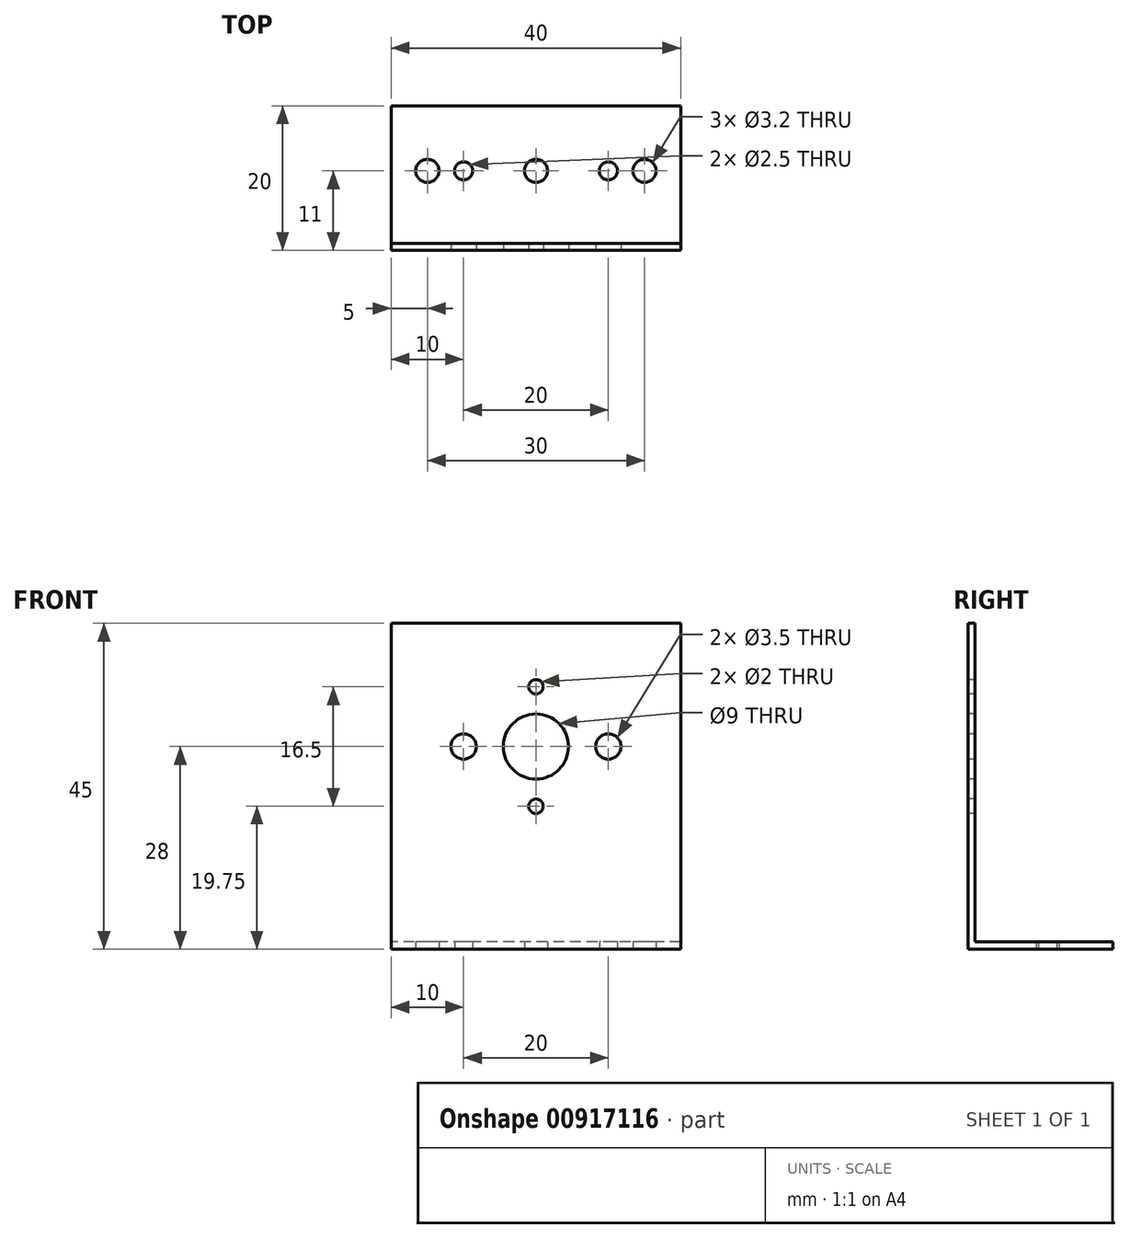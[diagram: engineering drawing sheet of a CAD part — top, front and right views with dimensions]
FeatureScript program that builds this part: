
annotation { "Feature Type Name" : "Feature", "Feature Type Description" : "" }
export const myFeature = defineFeature(function(context is Context, id is Id, definition is map)
    precondition{}
    {
        {
            var Q0;
            Q0=qCreatedBy(makeId("Right.planeOp"),FACE);
            var sketch = newSketch(context, id + "F0", { "sketchPlane" : qUnion([Q0])});
            skLineSegment(sketch, "E0", {"start": v(0, 0) * mm, "end": v(0, 45) * mm});
            skLineSegment(sketch, "E1", {"start": v(0, 45) * mm, "end": v(1, 45) * mm});
            skLineSegment(sketch, "E2", {"start": v(1, 45) * mm, "end": v(1, 1) * mm});
            skLineSegment(sketch, "E3", {"start": v(1, 1) * mm, "end": v(20, 1) * mm});
            skLineSegment(sketch, "E4", {"start": v(20, 1) * mm, "end": v(20, 0) * mm});
            skLineSegment(sketch, "E5", {"start": v(20, 0) * mm, "end": v(0, 0) * mm});
            skSolve(sketch);
        }
        {
            var Q0;
            Q0=makeQuery(id+"F0.imprint","IMPRINT",FACE,{"disambiguationData":[TD([[makeQuery(id+"F0.imprint","IMPRINT",EDGE,{"derivedFrom":sQuery(id+"F0.wireOp",EDGE,"E0")}),-1.0]])]});
            extrude(context, id + "F1", {"entities" : qUnion([Q0]), "depth" : 40 * mm, "offsetDistance" : 25.4 * mm});
        }
        {
            var Q0;
            Q0=makeQuery(id+"F1.opExtrude","SWEPT_FACE",FACE,{"disambiguationData":[OSD([sQuery(id+"F0.wireOp",EDGE,"E5")])]});
            var sketch = newSketch(context, id + "F2", { "sketchPlane" : qUnion([Q0])});
            skCircle(sketch, "E6", {"center": v(5, -11) * mm, "radius": 1.6 * mm});
            skCircle(sketch, "E7", {"center": v(10, -11) * mm, "radius": 1.25 * mm});
            skCircle(sketch, "E8", {"center": v(20, -11) * mm, "radius": 1.6 * mm});
            skCircle(sketch, "E9", {"center": v(30, -11) * mm, "radius": 1.25 * mm});
            skCircle(sketch, "E10", {"center": v(35, -11) * mm, "radius": 1.6 * mm});
            skPoint(sketch, "E11", {"position": v(20, 0) * mm});
            skSolve(sketch);
        }
        {
            var Q0;
            Q0=makeQuery(id+"F1.opExtrude","SWEPT_FACE",FACE,{"disambiguationData":[OSD([sQuery(id+"F0.wireOp",EDGE,"E0")])]});
            var sketch = newSketch(context, id + "F3", { "sketchPlane" : qUnion([Q0])});
            skCircle(sketch, "E12", {"center": v(20, 28) * mm, "radius": 4.5 * mm});
            skCircle(sketch, "E13", {"center": v(20, 36.25) * mm, "radius": 1 * mm});
            skCircle(sketch, "E14", {"center": v(20, 19.75) * mm, "radius": 1 * mm});
            skCircle(sketch, "E15", {"center": v(30, 28) * mm, "radius": 1.75 * mm});
            skCircle(sketch, "E16", {"center": v(10, 28) * mm, "radius": 1.75 * mm});
            skLineSegment(sketch, "E17", {"start": v(20, 36.25) * mm, "end": v(20, 19.75) * mm, "construction": true});
            skLineSegment(sketch, "E18", {"start": v(10, 28) * mm, "end": v(30, 28) * mm, "construction": true});
            skLineSegment(sketch, "E19", {"start": v(20, 45) * mm, "end": v(20, 0) * mm, "construction": true});
            skSolve(sketch);
        }
        {
            var Q0;
            Q0=sQuery(id+"F3.wireOp",VERTEX,"E18.start");
            var Q1;
            Q1=sQuery(id+"F3.wireOp",VERTEX,"E18.end");
            var Q2;
            Q2=makeQuery(id+"F1.opExtrude","SWEPT_BODY",BODY,{"disambiguationData":[OSD([sQuery(id+"F0.wireOp",EDGE,"E0"),sQuery(id+"F0.wireOp",EDGE,"E1"),sQuery(id+"F0.wireOp",EDGE,"E2"),sQuery(id+"F0.wireOp",EDGE,"E3"),sQuery(id+"F0.wireOp",EDGE,"E4"),sQuery(id+"F0.wireOp",EDGE,"E5")])]});
            hole(context, id + "F4", {"style" : HoleStyle.SIMPLE, "endStyle" : HoleEndStyle.THROUGH, "holeDiameter" : 3.5 * mm, "majorDiameter" : 6.35 * mm, "isTappedThrough" : true, "tappedDepth" : 12.7 * mm, "tapClearance" : 3, "locations" : qUnion([Q0, Q1]), "scope" : qUnion([Q2])});
        }
        {
            var Q0;
            Q0=sQuery(id+"F3.wireOp",VERTEX,"E12.center");
            var Q1;
            Q1=makeQuery(id+"F1.opExtrude","SWEPT_BODY",BODY,{"disambiguationData":[OSD([sQuery(id+"F0.wireOp",EDGE,"E0"),sQuery(id+"F0.wireOp",EDGE,"E1"),sQuery(id+"F0.wireOp",EDGE,"E2"),sQuery(id+"F0.wireOp",EDGE,"E3"),sQuery(id+"F0.wireOp",EDGE,"E4"),sQuery(id+"F0.wireOp",EDGE,"E5")])]});
            hole(context, id + "F5", {"style" : HoleStyle.SIMPLE, "endStyle" : HoleEndStyle.THROUGH, "holeDiameter" : 9 * mm, "majorDiameter" : 6.35 * mm, "isTappedThrough" : true, "tappedDepth" : 12.7 * mm, "tapClearance" : 3, "locations" : qUnion([Q0]), "scope" : qUnion([Q1])});
        }
        {
            var Q0;
            Q0=sQuery(id+"F3.wireOp",VERTEX,"E17.end");
            var Q1;
            Q1=sQuery(id+"F3.wireOp",VERTEX,"E17.start");
            var Q2;
            Q2=makeQuery(id+"F1.opExtrude","SWEPT_BODY",BODY,{"disambiguationData":[OSD([sQuery(id+"F0.wireOp",EDGE,"E0"),sQuery(id+"F0.wireOp",EDGE,"E1"),sQuery(id+"F0.wireOp",EDGE,"E2"),sQuery(id+"F0.wireOp",EDGE,"E3"),sQuery(id+"F0.wireOp",EDGE,"E4"),sQuery(id+"F0.wireOp",EDGE,"E5")])]});
            hole(context, id + "F6", {"style" : HoleStyle.SIMPLE, "endStyle" : HoleEndStyle.THROUGH, "holeDiameter" : 2 * mm, "majorDiameter" : 6.35 * mm, "isTappedThrough" : true, "tappedDepth" : 12.7 * mm, "tapClearance" : 3, "locations" : qUnion([Q0, Q1]), "scope" : qUnion([Q2])});
        }
        {
            var Q0;
            Q0=sQuery(id+"F2.wireOp",VERTEX,"E6.center");
            var Q1;
            Q1=sQuery(id+"F2.wireOp",VERTEX,"E8.center");
            var Q2;
            Q2=sQuery(id+"F2.wireOp",VERTEX,"E10.center");
            var Q3;
            Q3=makeQuery(id+"F1.opExtrude","SWEPT_BODY",BODY,{"disambiguationData":[OSD([sQuery(id+"F0.wireOp",EDGE,"E0"),sQuery(id+"F0.wireOp",EDGE,"E1"),sQuery(id+"F0.wireOp",EDGE,"E2"),sQuery(id+"F0.wireOp",EDGE,"E3"),sQuery(id+"F0.wireOp",EDGE,"E4"),sQuery(id+"F0.wireOp",EDGE,"E5")])]});
            hole(context, id + "F7", {"style" : HoleStyle.SIMPLE, "endStyle" : HoleEndStyle.THROUGH, "holeDiameter" : 3.2 * mm, "majorDiameter" : 6.35 * mm, "isTappedThrough" : true, "tappedDepth" : 12.7 * mm, "tapClearance" : 3, "locations" : qUnion([Q0, Q1, Q2]), "scope" : qUnion([Q3])});
        }
        {
            var Q0;
            Q0=sQuery(id+"F2.wireOp",VERTEX,"E7.center");
            var Q1;
            Q1=sQuery(id+"F2.wireOp",VERTEX,"E9.center");
            var Q2;
            Q2=makeQuery(id+"F1.opExtrude","SWEPT_BODY",BODY,{"disambiguationData":[OSD([sQuery(id+"F0.wireOp",EDGE,"E0"),sQuery(id+"F0.wireOp",EDGE,"E1"),sQuery(id+"F0.wireOp",EDGE,"E2"),sQuery(id+"F0.wireOp",EDGE,"E3"),sQuery(id+"F0.wireOp",EDGE,"E4"),sQuery(id+"F0.wireOp",EDGE,"E5")])]});
            hole(context, id + "F8", {"style" : HoleStyle.SIMPLE, "endStyle" : HoleEndStyle.THROUGH, "holeDiameter" : 2.5 * mm, "majorDiameter" : 6.35 * mm, "isTappedThrough" : true, "tappedDepth" : 12.7 * mm, "tapClearance" : 3, "locations" : qUnion([Q0, Q1]), "scope" : qUnion([Q2])});
        }
    });
